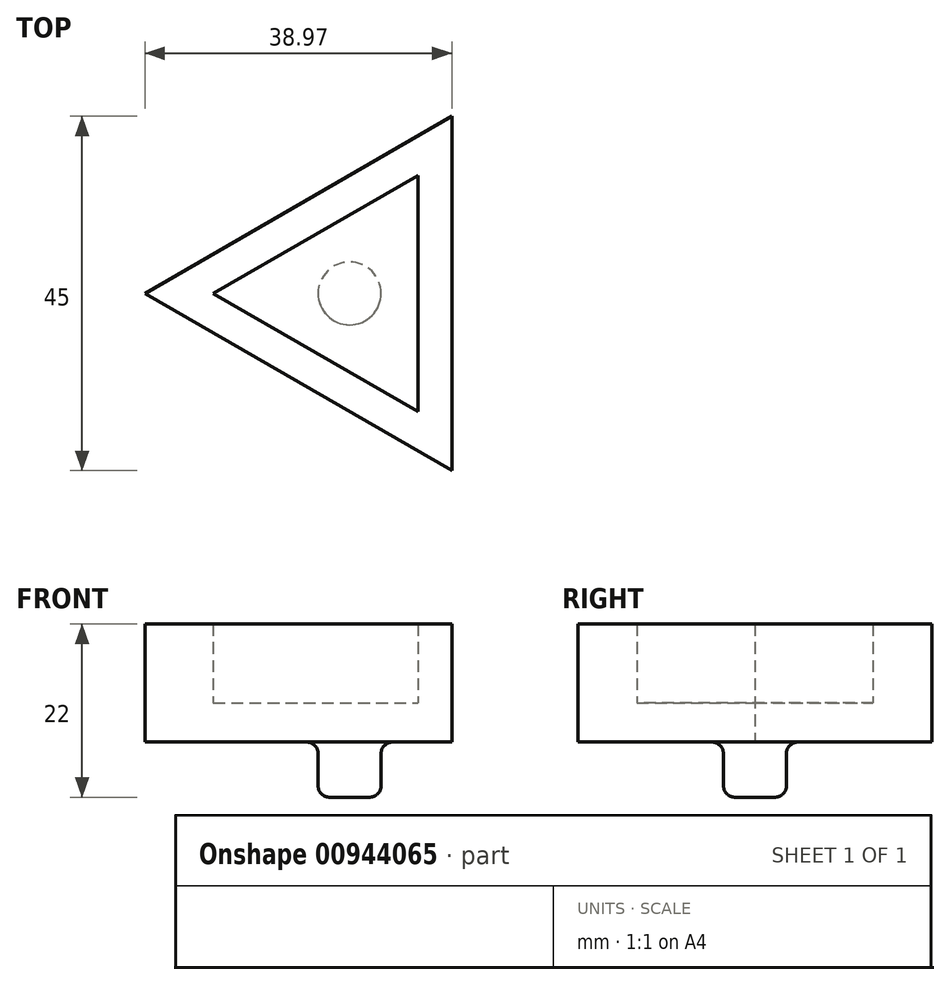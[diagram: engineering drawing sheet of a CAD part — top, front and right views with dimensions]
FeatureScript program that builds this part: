
annotation { "Feature Type Name" : "Feature", "Feature Type Description" : "" }
export const myFeature = defineFeature(function(context is Context, id is Id, definition is map)
    precondition{}
    {
        {
            var Q0;
            Q0=qCreatedBy(makeId("Top.planeOp"),FACE);
            var sketch = newSketch(context, id + "F0", { "sketchPlane" : qUnion([Q0])});
            skCircle(sketch, "E0.cCircle", {"center": v(0, 0) * mm, "radius": 8.66 * mm, "construction": true});
            skLineSegment(sketch, "E0.0", {"start": v(8.66, 15) * mm, "end": v(8.66, -15) * mm});
            skLineSegment(sketch, "E0.1", {"start": v(8.66, -15) * mm, "end": v(-17.32, 0) * mm});
            skLineSegment(sketch, "E0.2", {"start": v(-17.32, 0) * mm, "end": v(8.66, 15) * mm});
            skPoint(sketch, "E0.0.midPoint", {"position": v(8.66, 0) * mm});
            skCircle(sketch, "E1.cCircle", {"center": v(0, 0) * mm, "radius": 13 * mm, "construction": true});
            skLineSegment(sketch, "E1.0", {"start": v(13, 22.5) * mm, "end": v(13, -22.5) * mm});
            skLineSegment(sketch, "E1.1", {"start": v(13, -22.5) * mm, "end": v(-25.98, 0) * mm});
            skLineSegment(sketch, "E1.2", {"start": v(-25.98, 0) * mm, "end": v(13, 22.5) * mm});
            skPoint(sketch, "E1.0.midPoint", {"position": v(13, 0) * mm});
            skSolve(sketch);
        }
        {
            var Q0;
            Q0 = qSketchRegion(id + "F0", true);
            extrude(context, id + "F1", {"entities" : qUnion([Q0]), "depth" : 10 * mm, "offsetDistance" : 25 * mm});
        }
        {
            var Q0;
            Q0=makeQuery(id+"F0.imprint","IMPRINT",FACE,{"disambiguationData":[TD([[makeQuery(id+"F0.imprint","IMPRINT",EDGE,{"derivedFrom":sQuery(id+"F0.wireOp",EDGE,"E0.0")}),1.0]])]});
            var Q1;
            Q1=makeQuery(id+"F0.imprint","IMPRINT",FACE,{"disambiguationData":[TD([[makeQuery(id+"F0.imprint","IMPRINT",EDGE,{"derivedFrom":sQuery(id+"F0.wireOp",EDGE,"E0.0")}),-1.0]])]});
            extrude(context, id + "F2", {"entities" : qUnion([Q0, Q1]), "operationType" : NewBodyOperationType.ADD, "oppositeDirection" : true, "depth" : 5 * mm, "offsetDistance" : 25 * mm});
        }
        {
            var Q0;
            Q0=makeQuery(id+"F2.opExtrude","CAP_FACE",FACE,{"disambiguationData":[OSD([sQuery(id+"F0.wireOp",EDGE,"E1.0"),sQuery(id+"F0.wireOp",EDGE,"E1.1"),sQuery(id+"F0.wireOp",EDGE,"E1.2")])],"isStart":false});
            var sketch = newSketch(context, id + "F3", { "sketchPlane" : qUnion([Q0])});
            skCircle(sketch, "E2", {"center": v(0, 0) * mm, "radius": 4 * mm});
            skSolve(sketch);
        }
        {
            var Q0;
            Q0=makeQuery(id+"F3.imprint","IMPRINT",FACE,{"disambiguationData":[TD([[makeQuery(id+"F3.imprint","IMPRINT",EDGE,{"derivedFrom":sQuery(id+"F3.wireOp",EDGE,"E2")}),1.0]])]});
            extrude(context, id + "F4", {"entities" : qUnion([Q0]), "operationType" : NewBodyOperationType.ADD, "depth" : 7 * mm, "offsetDistance" : 25 * mm});
        }
        {
            var Q0;
            Q0=makeQuery(id+"F4.opExtrude","SWEPT_FACE",FACE,{"disambiguationData":[OSD([sQuery(id+"F3.wireOp",EDGE,"E2")])]});
            fillet(context, id + "F5", {"entities" : qUnion([Q0]), "radius" : 1.45 * mm, "tangentPropagation" : true, "allowEdgeOverflow" : false});
        }
    });
